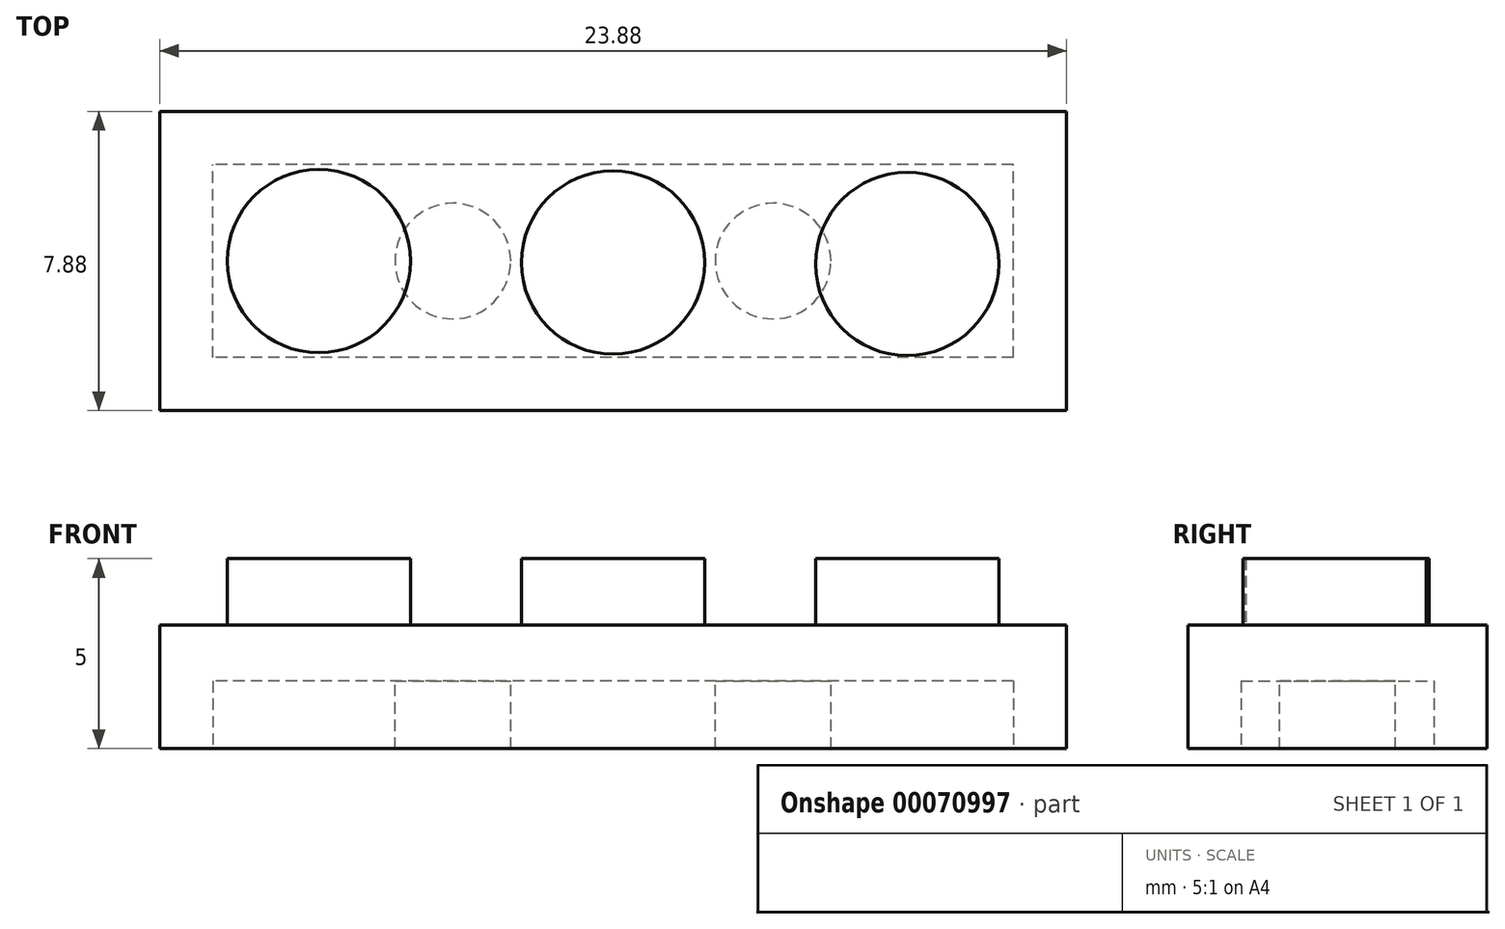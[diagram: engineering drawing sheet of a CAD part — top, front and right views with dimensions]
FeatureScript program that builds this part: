
annotation { "Feature Type Name" : "Feature", "Feature Type Description" : "" }
export const myFeature = defineFeature(function(context is Context, id is Id, definition is map)
    precondition{}
    {
        {
            var Q0;
            Q0=qCreatedBy(makeId("Top.planeOp"),FACE);
            var sketch = newSketch(context, id + "F0", { "sketchPlane" : qUnion([Q0])});
            skLineSegment(sketch, "E0.rect.bottom", {"start": v(11.94, -3.94) * mm, "end": v(-11.94, -3.94) * mm});
            skLineSegment(sketch, "E0.rect.top", {"start": v(11.94, 3.94) * mm, "end": v(-11.94, 3.94) * mm});
            skLineSegment(sketch, "E0.rect.left", {"start": v(11.94, -3.94) * mm, "end": v(11.94, 3.94) * mm});
            skLineSegment(sketch, "E0.rect.right", {"start": v(-11.94, -3.94) * mm, "end": v(-11.94, 3.94) * mm});
            skPoint(sketch, "E0.rect.middle", {"position": v(0, 0) * mm});
            skSolve(sketch);
        }
        {
            var Q0;
            Q0 = qSketchRegion(id + "F0", true);
            extrude(context, id + "F1", {"entities" : qUnion([Q0]), "depth" : 3.25 * mm});
        }
        {
            var Q0;
            Q0=makeQuery(id+"F1.opExtrude","CAP_FACE",FACE,{"disambiguationData":[OSD([sQuery(id+"F0.wireOp",EDGE,"E0.rect.bottom"),sQuery(id+"F0.wireOp",EDGE,"E0.rect.top"),sQuery(id+"F0.wireOp",EDGE,"E0.rect.left"),sQuery(id+"F0.wireOp",EDGE,"E0.rect.right")])],"isStart":true});
            var sketch = newSketch(context, id + "F2", { "sketchPlane" : qUnion([Q0])});
            skLineSegment(sketch, "E1.rect.bottom", {"start": v(10.54, 2.54) * mm, "end": v(-10.54, 2.54) * mm});
            skLineSegment(sketch, "E1.rect.top", {"start": v(10.54, -2.54) * mm, "end": v(-10.54, -2.54) * mm});
            skLineSegment(sketch, "E1.rect.left", {"start": v(10.54, 2.54) * mm, "end": v(10.54, -2.54) * mm});
            skLineSegment(sketch, "E1.rect.right", {"start": v(-10.54, 2.54) * mm, "end": v(-10.54, -2.54) * mm});
            skPoint(sketch, "E1.rect.middle", {"position": v(0, 0) * mm});
            skSolve(sketch);
        }
        {
            var Q0;
            Q0=makeQuery(id+"F2.imprint","IMPRINT",FACE,{"disambiguationData":[TD([[makeQuery(id+"F2.imprint","IMPRINT",EDGE,{"derivedFrom":sQuery(id+"F2.wireOp",EDGE,"E1.rect.bottom")}),1.0]])]});
            extrude(context, id + "F3", {"entities" : qUnion([Q0]), "operationType" : NewBodyOperationType.REMOVE, "oppositeDirection" : true, "depth" : 1.78 * mm});
        }
        {
            var Q0;
            Q0=makeQuery(id+"F1.opExtrude","CAP_FACE",FACE,{"disambiguationData":[OSD([sQuery(id+"F0.wireOp",EDGE,"E0.rect.bottom"),sQuery(id+"F0.wireOp",EDGE,"E0.rect.top"),sQuery(id+"F0.wireOp",EDGE,"E0.rect.left"),sQuery(id+"F0.wireOp",EDGE,"E0.rect.right")])],"isStart":false});
            var sketch = newSketch(context, id + "F4", { "sketchPlane" : qUnion([Q0])});
            skLineSegment(sketch, "E2", {"start": v(-11.94, 0) * mm, "end": v(-7.75, 0) * mm});
            skCircle(sketch, "E3", {"center": v(-7.75, 0) * mm, "radius": 2.41 * mm});
            skCircle(sketch, "E4.1.0.0", {"center": v(0, -0.04) * mm, "radius": 2.41 * mm});
            skCircle(sketch, "E4.2.0.0", {"center": v(7.75, -0.08) * mm, "radius": 2.41 * mm});
            skLineSegment(sketch, "E4.direction1", {"start": v(-7.75, 0) * mm, "end": v(0, -0.04) * mm, "construction": true});
            skSolve(sketch);
        }
        {
            var Q0;
            Q0=makeQuery(id+"F4.imprint","IMPRINT",FACE,{"disambiguationData":[TD([[makeQuery(id+"F4.imprint","IMPRINT",EDGE,{"derivedFrom":sQuery(id+"F4.wireOp",EDGE,"E3")}),1.0]])]});
            var Q1;
            Q1=makeQuery(id+"F4.imprint","IMPRINT",FACE,{"disambiguationData":[TD([[makeQuery(id+"F4.imprint","IMPRINT",EDGE,{"derivedFrom":sQuery(id+"F4.wireOp",EDGE,"E4.1.0.0")}),1.0]])]});
            var Q2;
            Q2=makeQuery(id+"F4.imprint","IMPRINT",FACE,{"disambiguationData":[TD([[makeQuery(id+"F4.imprint","IMPRINT",EDGE,{"derivedFrom":sQuery(id+"F4.wireOp",EDGE,"E4.2.0.0")}),1.0]])]});
            extrude(context, id + "F5", {"entities" : qUnion([Q0, Q1, Q2]), "operationType" : NewBodyOperationType.ADD, "depth" : 1.75 * mm});
        }
        {
            var Q0;
            Q0=makeQuery(id+"F3.boolean.opBoolean","COPY",FACE,{"derivedFrom":makeQuery(id+"F3.opExtrude","CAP_FACE",FACE,{"disambiguationData":[OSD([sQuery(id+"F2.wireOp",EDGE,"E1.rect.bottom"),sQuery(id+"F2.wireOp",EDGE,"E1.rect.top"),sQuery(id+"F2.wireOp",EDGE,"E1.rect.left"),sQuery(id+"F2.wireOp",EDGE,"E1.rect.right")])],"isStart":false})});
            var sketch = newSketch(context, id + "F6", { "sketchPlane" : qUnion([Q0])});
            skLineSegment(sketch, "E5", {"start": v(-10.54, 0) * mm, "end": v(-4.22, 0) * mm});
            skPoint(sketch, "E5.endSnap0", {"position": v(-10.54, 0) * mm});
            skCircle(sketch, "E6", {"center": v(-4.22, 0) * mm, "radius": 1.52 * mm});
            skCircle(sketch, "E7.1.0.0", {"center": v(4.22, 0) * mm, "radius": 1.52 * mm});
            skLineSegment(sketch, "E7.direction1", {"start": v(-4.22, 0) * mm, "end": v(4.22, 0) * mm, "construction": true});
            skSolve(sketch);
        }
        {
            var Q0;
            Q0=makeQuery(id+"F6.imprint","IMPRINT",FACE,{"disambiguationData":[TD([[makeQuery(id+"F6.imprint","IMPRINT",EDGE,{"derivedFrom":sQuery(id+"F6.wireOp",EDGE,"E6")}),1.0]])]});
            var Q1;
            Q1=makeQuery(id+"F6.imprint","IMPRINT",FACE,{"disambiguationData":[TD([[makeQuery(id+"F6.imprint","IMPRINT",EDGE,{"derivedFrom":sQuery(id+"F6.wireOp",EDGE,"E7.1.0.0")}),1.0]])]});
            extrude(context, id + "F7", {"entities" : qUnion([Q0, Q1]), "operationType" : NewBodyOperationType.ADD, "depth" : 1.78 * mm});
        }
    });
